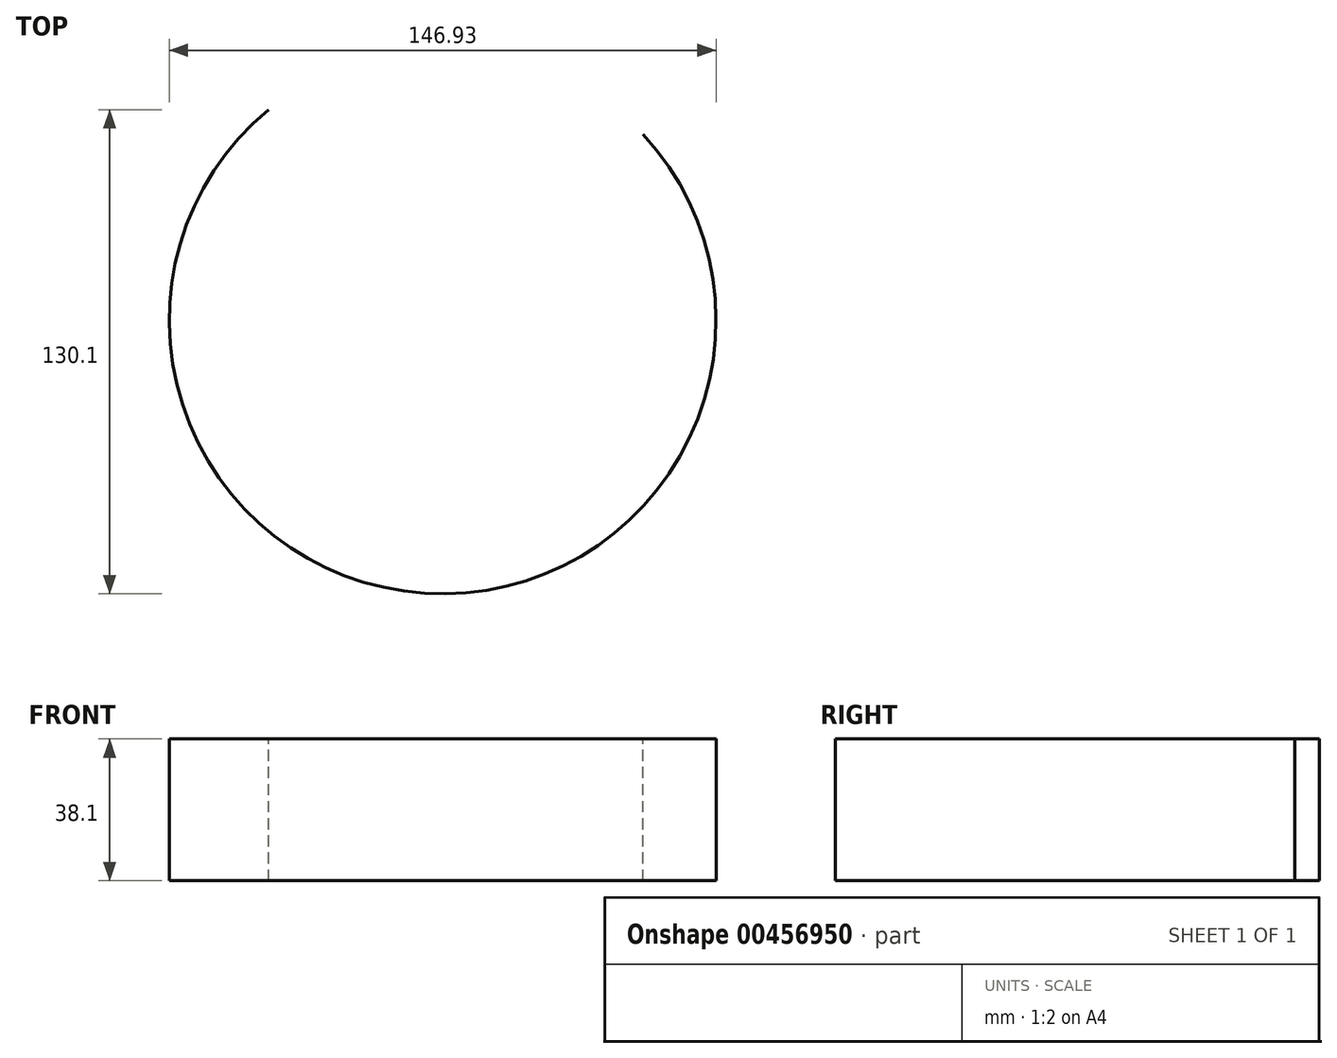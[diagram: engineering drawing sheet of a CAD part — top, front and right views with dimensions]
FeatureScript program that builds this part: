
annotation { "Feature Type Name" : "Feature", "Feature Type Description" : "" }
export const myFeature = defineFeature(function(context is Context, id is Id, definition is map)
    precondition{}
    {
        {
            var Q0;
            Q0=qCreatedBy(makeId("Top.planeOp"),FACE);
            var sketch = newSketch(context, id + "F0", { "sketchPlane" : qUnion([Q0])});
            skArc(sketch, "E0", {"start": v(-50.2, 58.09) * mm, "mid": v(-8.25, -71.85) * mm, "end": v(50.41, 51.45) * mm});
            skSolve(sketch);
        }
        {
            var Q0;
            Q0=sQuery(id+"F0.wireOp",EDGE,"E0");
            extrude(context, id + "F1", {"bodyType" : ToolBodyType.SURFACE, "surfaceEntities" : qUnion([Q0]), "depth" : 38.1 * mm});
        }
    });
